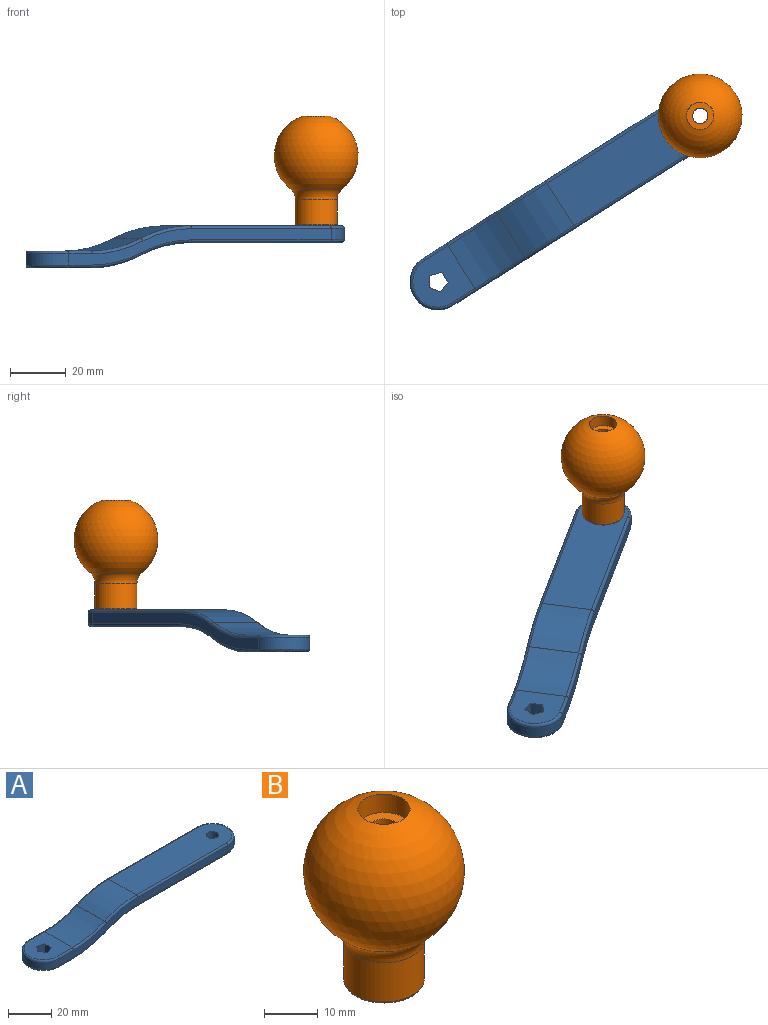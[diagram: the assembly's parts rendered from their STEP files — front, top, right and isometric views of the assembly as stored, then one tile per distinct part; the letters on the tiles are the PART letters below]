
ASSEMBLY  parts=2 mates=1
PART A: 44 faces, bbox 132.5x21.6x23.4 mm
  f0: cylinder r=10mm len=20mm, axis (0,0,-1), area 125.7mm2, adj f7,f8,f27,f32
  f1: plane 18.92x18mm, normal (0,0,1), area 273.7mm2, adj f9,f10,f11,f12,f13,f17,f25,f27
  f2: plane 18.92x18mm, normal (0,0,-1), area 273.7mm2, adj f9,f10,f11,f12,f13,f14,f32,f33
  f3: plane 18x0.04mm, normal (0.41,0,-0.91), area 0.7mm2, adj f14,f15,f37,f38
  f4: plane 68.05x18mm, normal (0,0,-1), area 1166.4mm2, adj f15,f19,f41,f42,f43
  f5: plane 68.05x18mm, normal (0,0,1), area 1166.4mm2, adj f16,f19,f22,f24,f26
  f6: plane 18x0.04mm, normal (-0.41,0,0.91), area 0.7mm2, adj f16,f17,f21,f30
  f7: plane 110.87x13mm, normal (0,-1,0), area 440.9mm2, adj f0,f18,f20,f21,f22,f23,f25,f34
  f8: plane 110.87x13mm, normal (0,1,0), area 440.9mm2, adj f0,f18,f26,f28,f29,f30,f31,f33
  f9: plane 6x4.32mm, normal (-1,0,0), area 25.9mm2, adj f1,f2,f10,f12
  f10: plane 6x4.11mm, normal (-0.31,-0.95,0), area 25.9mm2, adj f1,f2,f9,f11
  f11: plane 6x3.5mm, normal (0.81,-0.59,0), area 25.9mm2, adj f1,f2,f10,f13
  f12: plane 6x4.11mm, normal (-0.31,0.95,0), area 25.9mm2, adj f1,f2,f9,f13
  f13: plane 6x3.5mm, normal (0.81,0.59,0), area 25.9mm2, adj f1,f2,f11,f12
  f14: cylinder r=51mm len=20.93mm, axis (0,1,0), area 388.2mm2, adj f2,f3,f35,f36
  f15: cylinder r=51mm len=20.93mm, axis (0,-1,0), area 388.2mm2, adj f3,f4,f39,f40
  f16: cylinder r=51mm len=20.93mm, axis (0,1,0), area 388.2mm2, adj f5,f6,f20,f28
  f17: cylinder r=51mm len=20.93mm, axis (0,1,0), area 388.2mm2, adj f1,f6,f23,f31
  f18: cylinder r=10mm len=20mm, axis (0,0,-1), area 125.7mm2, adj f7,f8,f24,f43
  f19: cylinder r=2.75mm len=6mm, axis (0,0,1), area 103.7mm2, adj f4,f5
  f20: torus R=50mm, axis (0,-1,0), area 33.6mm2, adj f7,f16,f21,f22
  f21: cylinder r=1mm len=1mm, axis (0.91,0,0.41), area 0.1mm2, adj f6,f7,f20,f23
  f22: cylinder r=1mm len=59.05mm, axis (1,0,0), area 92.8mm2, adj f5,f7,f20,f24
  f23: torus R=52mm, axis (0,-1,0), area 34.1mm2, adj f7,f17,f21,f25
  f24: torus R=9mm, axis (0,0,-1), area 47.6mm2, adj f5,f18,f22,f26
  f25: cylinder r=1mm len=9.92mm, axis (-1,0,0), area 15.6mm2, adj f1,f7,f23,f27
  f26: cylinder r=1mm len=59.05mm, axis (-1,0,0), area 92.8mm2, adj f5,f8,f24,f28
  f27: torus R=9mm, axis (0,0,1), area 47.6mm2, adj f0,f1,f25,f29
  f28: torus R=50mm, axis (0,-1,0), area 33.6mm2, adj f8,f16,f26,f30
  f29: cylinder r=1mm len=9.92mm, axis (1,0,0), area 15.6mm2, adj f1,f8,f27,f31
  f30: cylinder r=1mm len=1mm, axis (-0.91,0,-0.41), area 0.1mm2, adj f6,f8,f28,f31
  f31: torus R=52mm, axis (0,-1,0), area 34.1mm2, adj f8,f17,f29,f30
  f32: torus R=9mm, axis (0,0,1), area 47.6mm2, adj f0,f2,f33,f34
  f33: cylinder r=1mm len=9.92mm, axis (1,0,0), area 15.6mm2, adj f2,f8,f32,f35
  f34: cylinder r=1mm len=9.92mm, axis (-1,0,0), area 15.6mm2, adj f2,f7,f32,f36
  f35: torus R=50mm, axis (0,-1,0), area 33.6mm2, adj f8,f14,f33,f37
  f36: torus R=50mm, axis (0,-1,0), area 33.6mm2, adj f7,f14,f34,f38
  f37: cylinder r=1mm len=1mm, axis (0.91,0,0.41), area 0.1mm2, adj f3,f8,f35,f39
  f38: cylinder r=1mm len=1mm, axis (-0.91,0,-0.41), area 0.1mm2, adj f3,f7,f36,f40
  f39: torus R=52mm, axis (0,-1,0), area 34.1mm2, adj f8,f15,f37,f41
  f40: torus R=52mm, axis (0,-1,0), area 34.1mm2, adj f7,f15,f38,f42
  f41: cylinder r=1mm len=59.05mm, axis (1,0,0), area 92.8mm2, adj f4,f8,f39,f43
  f42: cylinder r=1mm len=59.05mm, axis (-1,0,0), area 92.8mm2, adj f4,f7,f40,f43
  f43: torus R=9mm, axis (0,0,1), area 47.6mm2, adj f4,f18,f41,f42
PART B: 8 faces, bbox 30x30x39.2 mm
  f0: sphere r=15mm, area 2440.6mm2, adj f5,f6
  f1: cylinder r=7.5mm len=15mm, axis (0,0,-1), area 418.8mm2, adj f6,f7
  f2: plane 14x14mm, normal (0,0,-1), area 130.2mm2, adj f3,f7
  f3: cylinder r=2.75mm len=35mm, axis (0,0,1), area 604.8mm2, adj f2,f4
  f4: plane 9.75x9.75mm, normal (0,0,1), area 50.9mm2, adj f3,f5
  f5: cylinder r=4.88mm len=9.75mm, axis (0,0,1), area 128.2mm2, adj f0,f4
  f6: torus R=12.5mm, axis (0,0,1), area 229.1mm2, adj f0,f1
  f7: torus R=7mm, axis (0,0,1), area 36.1mm2, adj f1,f2
PLACE A rot(axis=(0,0,1),32.3deg) t=(0,0,0)mm
PLACE B rot(axis=(0,0,-1),73.7deg) t=(93.7,59.27,15)mm
MATE revolute A.f19 <-> B.f3  axis (0,0,1) through (93.7,59.27,15)mm
